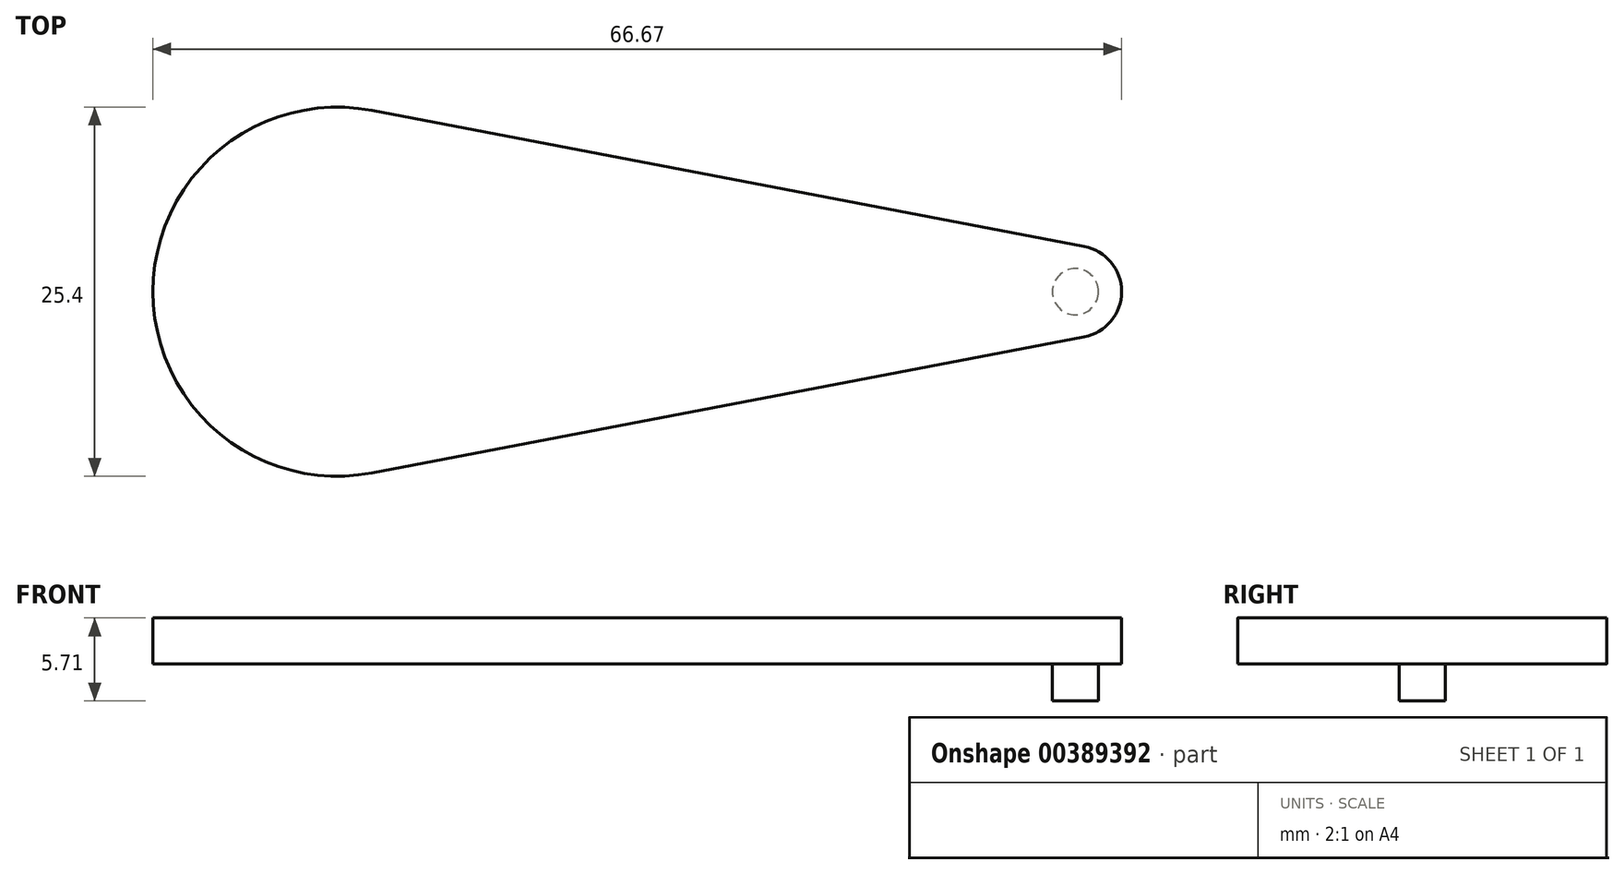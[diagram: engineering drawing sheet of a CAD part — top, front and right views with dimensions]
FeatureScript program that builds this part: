
annotation { "Feature Type Name" : "Feature", "Feature Type Description" : "" }
export const myFeature = defineFeature(function(context is Context, id is Id, definition is map)
    precondition{}
    {
        {
            var Q0;
            Q0=qCreatedBy(makeId("Top.planeOp"),FACE);
            var sketch = newSketch(context, id + "F0", { "sketchPlane" : qUnion([Q0])});
            skArc(sketch, "E0", {"start": v(0.6, -3.12) * mm, "mid": v(3.18, 0) * mm, "end": v(0.6, 3.12) * mm});
            skArc(sketch, "E1", {"start": v(-48.42, 12.47) * mm, "mid": v(-63.5, 0) * mm, "end": v(-48.42, -12.47) * mm});
            skLineSegment(sketch, "E2", {"start": v(-48.42, 12.47) * mm, "end": v(0.6, 3.12) * mm});
            skLineSegment(sketch, "E3", {"start": v(-48.42, -12.47) * mm, "end": v(0.6, -3.12) * mm});
            skCircle(sketch, "E4", {"center": v(0, 0) * mm, "radius": 1.59 * mm});
            skSolve(sketch);
        }
        {
            var Q0;
            Q0=makeQuery(id+"F0.imprint","IMPRINT",FACE,{"disambiguationData":[TD([[makeQuery(id+"F0.imprint","IMPRINT",EDGE,{"derivedFrom":sQuery(id+"F0.wireOp",EDGE,"E0")}),1.0]])]});
            var Q1;
            Q1=makeQuery(id+"F0.imprint","IMPRINT",FACE,{"disambiguationData":[TD([[makeQuery(id+"F0.imprint","IMPRINT",EDGE,{"derivedFrom":sQuery(id+"F0.wireOp",EDGE,"E4")}),1.0]])]});
            extrude(context, id + "F1", {"entities" : qUnion([Q0, Q1]), "depth" : 3.17 * mm});
        }
        {
            var Q0;
            Q0=makeQuery(id+"F0.imprint","IMPRINT",FACE,{"disambiguationData":[TD([[makeQuery(id+"F0.imprint","IMPRINT",EDGE,{"derivedFrom":sQuery(id+"F0.wireOp",EDGE,"E4")}),1.0]])]});
            extrude(context, id + "F2", {"entities" : qUnion([Q0]), "operationType" : NewBodyOperationType.ADD, "oppositeDirection" : true, "depth" : 2.54 * mm});
        }
    });
